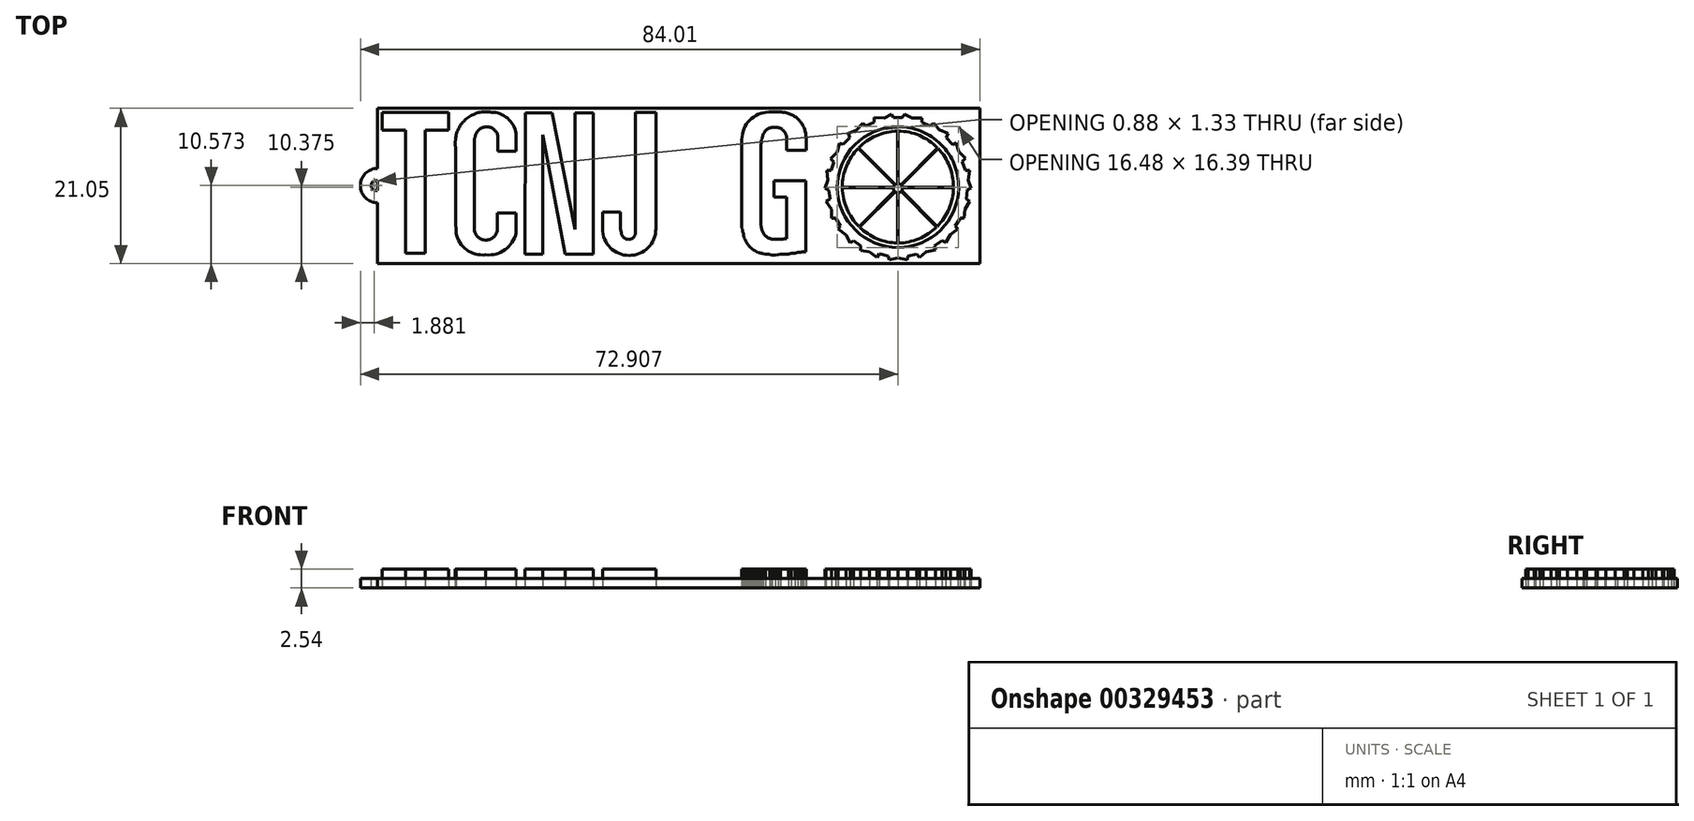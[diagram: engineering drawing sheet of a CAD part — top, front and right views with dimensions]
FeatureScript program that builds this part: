
annotation { "Feature Type Name" : "Feature", "Feature Type Description" : "" }
export const myFeature = defineFeature(function(context is Context, id is Id, definition is map)
    precondition{}
    {
        {
            var Q0;
            Q0=qCreatedBy(makeId("Top.planeOp"),FACE);
            var sketch = newSketch(context, id + "F0", { "sketchPlane" : qUnion([Q0])});
            skLineSegment(sketch, "E0", {"start": v(-44.56, 10.68) * mm, "end": v(-35.54, 10.68) * mm});
            skLineSegment(sketch, "E1", {"start": v(-35.54, 8.27) * mm, "end": v(-38.72, 8.27) * mm});
            skLineSegment(sketch, "E2", {"start": v(-38.72, 8.27) * mm, "end": v(-38.72, -8.39) * mm});
            skLineSegment(sketch, "E3", {"start": v(-38.72, -8.39) * mm, "end": v(-41.34, -8.39) * mm});
            skLineSegment(sketch, "E4", {"start": v(-41.34, -8.39) * mm, "end": v(-41.34, 8.27) * mm});
            skLineSegment(sketch, "E5", {"start": v(-44.56, 10.68) * mm, "end": v(-44.56, 8.3) * mm});
            skLineSegment(sketch, "E6", {"start": v(-44.56, 8.3) * mm, "end": v(-41.34, 8.27) * mm});
            skLineSegment(sketch, "E7", {"start": v(-35.54, 10.68) * mm, "end": v(-35.54, 8.27) * mm});
            skLineSegment(sketch, "E8", {"start": v(-28.83, 5.45) * mm, "end": v(-26.4, 5.45) * mm});
            skLineSegment(sketch, "E9", {"start": v(-26.4, 5.45) * mm, "end": v(-26.4, 7.84) * mm});
            skArc(sketch, "E10", {"start": v(-26.4, 7.84) * mm, "mid": v(-27.53, 9.9) * mm, "end": v(-29.75, 10.73) * mm});
            skArc(sketch, "E11", {"start": v(-29.75, 10.73) * mm, "mid": v(-32.98, 9.95) * mm, "end": v(-34.6, 7.04) * mm});
            skArc(sketch, "E12", {"start": v(-34.6, 7.04) * mm, "mid": v(-34.62, 6.47) * mm, "end": v(-34.6, 5.9) * mm});
            skLineSegment(sketch, "E13", {"start": v(-34.6, 5.9) * mm, "end": v(-34.6, -3.94) * mm});
            skArc(sketch, "E14", {"start": v(-28.83, 7.44) * mm, "mid": v(-30.37, 8.75) * mm, "end": v(-31.9, 7.43) * mm});
            skLineSegment(sketch, "E15", {"start": v(-28.83, 7.44) * mm, "end": v(-28.83, 5.45) * mm});
            skArc(sketch, "E16", {"start": v(-31.9, 7.43) * mm, "mid": v(-32.02, 7.1) * mm, "end": v(-32.05, 6.76) * mm});
            skLineSegment(sketch, "E17", {"start": v(-32.05, 6.76) * mm, "end": v(-32.05, -3.9) * mm});
            skLineSegment(sketch, "E18", {"start": v(-32.05, -3.9) * mm, "end": v(-32.05, -5.06) * mm});
            skArc(sketch, "E19", {"start": v(-32.05, -5.06) * mm, "mid": v(-30.48, -6.63) * mm, "end": v(-28.9, -5.06) * mm});
            skLineSegment(sketch, "E20", {"start": v(-28.9, -5.06) * mm, "end": v(-28.9, -2.93) * mm});
            skLineSegment(sketch, "E21", {"start": v(-28.9, -2.93) * mm, "end": v(-26.38, -2.93) * mm});
            skLineSegment(sketch, "E22", {"start": v(-26.38, -2.93) * mm, "end": v(-26.38, -5.66) * mm});
            skArc(sketch, "E23", {"start": v(-30.48, -8.61) * mm, "mid": v(-27.86, -7.93) * mm, "end": v(-26.38, -5.66) * mm});
            skArc(sketch, "E24", {"start": v(-34.5, -5.66) * mm, "mid": v(-33.08, -7.94) * mm, "end": v(-30.48, -8.61) * mm});
            skLineSegment(sketch, "E25", {"start": v(-34.6, -3.94) * mm, "end": v(-34.5, -5.66) * mm});
            skLineSegment(sketch, "E26", {"start": v(-25.23, 10.62) * mm, "end": v(-21.47, 10.62) * mm});
            skLineSegment(sketch, "E27", {"start": v(-21.47, 10.62) * mm, "end": v(-18.35, -5.14) * mm});
            skLineSegment(sketch, "E28", {"start": v(-18.35, -5.14) * mm, "end": v(-18.35, 10.66) * mm});
            skLineSegment(sketch, "E29", {"start": v(-18.35, 10.66) * mm, "end": v(-15.87, 10.66) * mm});
            skLineSegment(sketch, "E30", {"start": v(-15.87, 10.66) * mm, "end": v(-15.87, -8.5) * mm});
            skLineSegment(sketch, "E31", {"start": v(-15.87, -8.5) * mm, "end": v(-19.7, -8.5) * mm});
            skLineSegment(sketch, "E32", {"start": v(-19.7, -8.5) * mm, "end": v(-22.75, 7.66) * mm});
            skLineSegment(sketch, "E33", {"start": v(-22.75, 7.66) * mm, "end": v(-22.75, -8.5) * mm});
            skLineSegment(sketch, "E34", {"start": v(-22.75, -8.5) * mm, "end": v(-25.19, -8.5) * mm});
            skLineSegment(sketch, "E35", {"start": v(-25.19, -8.5) * mm, "end": v(-25.11, 10.62) * mm});
            skLineSegment(sketch, "E36", {"start": v(-10.17, 10.7) * mm, "end": v(-7.42, 10.7) * mm});
            skLineSegment(sketch, "E37", {"start": v(-7.42, 10.7) * mm, "end": v(-7.42, -5.1) * mm});
            skArc(sketch, "E38", {"start": v(-14.65, -5.1) * mm, "mid": v(-11.03, -8.7) * mm, "end": v(-7.42, -5.1) * mm});
            skLineSegment(sketch, "E39", {"start": v(-14.65, -5.1) * mm, "end": v(-14.65, -2.85) * mm});
            skLineSegment(sketch, "E40", {"start": v(-14.65, -2.85) * mm, "end": v(-12.2, -2.85) * mm});
            skLineSegment(sketch, "E41", {"start": v(-12.2, -2.85) * mm, "end": v(-12.2, -5.1) * mm});
            skLineSegment(sketch, "E42", {"start": v(-10.17, 10.7) * mm, "end": v(-10.17, -5.1) * mm});
            skLineSegment(sketch, "E43", {"start": v(-12.2, -5.1) * mm, "end": v(-12.11, -5.6) * mm});
            skLineSegment(sketch, "E44", {"start": v(-10.17, -5.1) * mm, "end": v(-10.17, -5.57) * mm});
            skArc(sketch, "E45", {"start": v(-12.11, -5.6) * mm, "mid": v(-11.12, -6.54) * mm, "end": v(-10.17, -5.57) * mm});
            skLineSegment(sketch, "E46", {"start": v(10.32, 5.53) * mm, "end": v(12.96, 5.53) * mm});
            skLineSegment(sketch, "E47", {"start": v(12.96, 5.53) * mm, "end": v(12.96, 7.18) * mm});
            skLineSegment(sketch, "E48", {"start": v(10.32, 5.53) * mm, "end": v(10.32, 7.18) * mm});
            skLineSegment(sketch, "E49", {"start": v(7.88, 10.74) * mm, "end": v(9.46, 10.74) * mm});
            skArc(sketch, "E50", {"start": v(12.96, 7.18) * mm, "mid": v(11.96, 9.7) * mm, "end": v(9.46, 10.74) * mm});
            skLineSegment(sketch, "E51", {"start": v(6.83, 6.3) * mm, "end": v(6.83, -4.43) * mm});
            skLineSegment(sketch, "E52", {"start": v(4.25, 7.04) * mm, "end": v(4.25, -4.85) * mm});
            skLineSegment(sketch, "E53", {"start": v(9.86, -6.5) * mm, "end": v(8.28, -6.5) * mm});
            skLineSegment(sketch, "E54", {"start": v(9.86, -6.5) * mm, "end": v(9.96, -6.44) * mm});
            skLineSegment(sketch, "E55", {"start": v(9.96, -6.44) * mm, "end": v(10.32, -6.44) * mm});
            skLineSegment(sketch, "E56", {"start": v(10.32, -6.44) * mm, "end": v(10.32, -0.84) * mm});
            skLineSegment(sketch, "E57", {"start": v(10.32, -0.84) * mm, "end": v(10.32, -0.8) * mm});
            skLineSegment(sketch, "E58", {"start": v(10.32, -0.8) * mm, "end": v(8.58, -0.8) * mm});
            skLineSegment(sketch, "E59", {"start": v(8.58, -0.8) * mm, "end": v(8.58, 1.43) * mm});
            skLineSegment(sketch, "E60", {"start": v(8.58, 1.43) * mm, "end": v(12.92, 1.43) * mm});
            skLineSegment(sketch, "E61", {"start": v(12.92, 1.43) * mm, "end": v(12.92, -8.2) * mm});
            skLineSegment(sketch, "E62", {"start": v(12.92, -8.2) * mm, "end": v(12.6, -8.2) * mm});
            skLineSegment(sketch, "E63", {"start": v(12.6, -8.2) * mm, "end": v(12.44, -8.25) * mm});
            skLineSegment(sketch, "E64", {"start": v(12.44, -8.25) * mm, "end": v(12.24, -8.3) * mm});
            skLineSegment(sketch, "E65", {"start": v(12.24, -8.3) * mm, "end": v(11.83, -8.3) * mm});
            skLineSegment(sketch, "E66", {"start": v(11.83, -8.3) * mm, "end": v(11.61, -8.38) * mm});
            skLineSegment(sketch, "E67", {"start": v(11.61, -8.38) * mm, "end": v(11.48, -8.42) * mm});
            skLineSegment(sketch, "E68", {"start": v(11.48, -8.42) * mm, "end": v(11.08, -8.42) * mm});
            skLineSegment(sketch, "E69", {"start": v(11.08, -8.42) * mm, "end": v(10.99, -8.42) * mm});
            skLineSegment(sketch, "E70", {"start": v(10.99, -8.42) * mm, "end": v(10.95, -8.42) * mm});
            skLineSegment(sketch, "E71", {"start": v(10.95, -8.42) * mm, "end": v(10.6, -8.54) * mm});
            skLineSegment(sketch, "E72", {"start": v(10.6, -8.54) * mm, "end": v(9.46, -8.54) * mm});
            skLineSegment(sketch, "E73", {"start": v(9.46, -8.54) * mm, "end": v(9.16, -8.58) * mm});
            skLineSegment(sketch, "E74", {"start": v(9.16, -8.58) * mm, "end": v(8.82, -8.65) * mm});
            skLineSegment(sketch, "E75", {"start": v(8.82, -8.65) * mm, "end": v(8.36, -8.65) * mm});
            skLineSegment(sketch, "E76", {"start": v(8.36, -8.65) * mm, "end": v(8.12, -8.58) * mm});
            skLineSegment(sketch, "E77", {"start": v(8.12, -8.58) * mm, "end": v(8.04, -8.55) * mm});
            skLineSegment(sketch, "E78", {"start": v(8.04, -8.55) * mm, "end": v(7.44, -8.55) * mm});
            skLineSegment(sketch, "E79", {"start": v(7.44, -8.55) * mm, "end": v(7.13, -8.45) * mm});
            skLineSegment(sketch, "E80", {"start": v(7.13, -8.45) * mm, "end": v(7.09, -8.43) * mm});
            skLineSegment(sketch, "E81", {"start": v(7.09, -8.43) * mm, "end": v(6.83, -8.43) * mm});
            skLineSegment(sketch, "E82", {"start": v(6.83, -8.43) * mm, "end": v(6.67, -8.32) * mm});
            skLineSegment(sketch, "E83", {"start": v(6.67, -8.32) * mm, "end": v(6.52, -8.32) * mm});
            skLineSegment(sketch, "E84", {"start": v(6.52, -8.32) * mm, "end": v(6.34, -8.21) * mm});
            skLineSegment(sketch, "E85", {"start": v(6.34, -8.21) * mm, "end": v(6.22, -8.21) * mm});
            skLineSegment(sketch, "E86", {"start": v(6.22, -8.21) * mm, "end": v(6.19, -8.16) * mm});
            skLineSegment(sketch, "E87", {"start": v(6.19, -8.16) * mm, "end": v(6.1, -8.09) * mm});
            skLineSegment(sketch, "E88", {"start": v(6.1, -8.09) * mm, "end": v(6, -8.09) * mm});
            skLineSegment(sketch, "E89", {"start": v(6, -8.09) * mm, "end": v(5.87, -7.97) * mm});
            skLineSegment(sketch, "E90", {"start": v(5.87, -7.97) * mm, "end": v(5.77, -7.94) * mm});
            skLineSegment(sketch, "E91", {"start": v(5.77, -7.94) * mm, "end": v(5.74, -7.85) * mm});
            skLineSegment(sketch, "E92", {"start": v(5.74, -7.85) * mm, "end": v(5.63, -7.85) * mm});
            skLineSegment(sketch, "E93", {"start": v(5.63, -7.85) * mm, "end": v(5.6, -7.74) * mm});
            skLineSegment(sketch, "E94", {"start": v(5.6, -7.74) * mm, "end": v(5.5, -7.74) * mm});
            skLineSegment(sketch, "E95", {"start": v(5.5, -7.74) * mm, "end": v(5.47, -7.64) * mm});
            skLineSegment(sketch, "E96", {"start": v(5.47, -7.64) * mm, "end": v(5.4, -7.64) * mm});
            skLineSegment(sketch, "E97", {"start": v(5.4, -7.64) * mm, "end": v(5.29, -7.53) * mm});
            skLineSegment(sketch, "E98", {"start": v(5.29, -7.53) * mm, "end": v(5.29, -7.48) * mm});
            skLineSegment(sketch, "E99", {"start": v(5.29, -7.48) * mm, "end": v(5.18, -7.38) * mm});
            skLineSegment(sketch, "E100", {"start": v(5.18, -7.38) * mm, "end": v(5.15, -7.38) * mm});
            skLineSegment(sketch, "E101", {"start": v(5.15, -7.38) * mm, "end": v(5.15, -7.33) * mm});
            skLineSegment(sketch, "E102", {"start": v(5.15, -7.33) * mm, "end": v(5.05, -7.26) * mm});
            skLineSegment(sketch, "E103", {"start": v(5.05, -7.26) * mm, "end": v(5.05, -7.14) * mm});
            skLineSegment(sketch, "E104", {"start": v(5.05, -7.14) * mm, "end": v(4.93, -7.03) * mm});
            skLineSegment(sketch, "E105", {"start": v(4.93, -7.03) * mm, "end": v(4.93, -6.95) * mm});
            skLineSegment(sketch, "E106", {"start": v(4.93, -6.95) * mm, "end": v(4.8, -6.87) * mm});
            skLineSegment(sketch, "E107", {"start": v(4.8, -6.87) * mm, "end": v(4.8, -6.75) * mm});
            skLineSegment(sketch, "E108", {"start": v(4.8, -6.75) * mm, "end": v(4.7, -6.65) * mm});
            skLineSegment(sketch, "E109", {"start": v(4.7, -6.65) * mm, "end": v(4.7, -6.51) * mm});
            skLineSegment(sketch, "E110", {"start": v(4.7, -6.51) * mm, "end": v(4.56, -6.34) * mm});
            skLineSegment(sketch, "E111", {"start": v(4.56, -6.34) * mm, "end": v(4.56, -6.19) * mm});
            skLineSegment(sketch, "E112", {"start": v(4.56, -6.19) * mm, "end": v(4.45, -6.1) * mm});
            skLineSegment(sketch, "E113", {"start": v(4.45, -6.1) * mm, "end": v(4.45, -5.75) * mm});
            skLineSegment(sketch, "E114", {"start": v(4.45, -5.75) * mm, "end": v(4.33, -5.48) * mm});
            skLineSegment(sketch, "E115", {"start": v(4.33, -5.48) * mm, "end": v(4.33, -5.18) * mm});
            skLineSegment(sketch, "E116", {"start": v(4.33, -5.18) * mm, "end": v(4.25, -4.97) * mm});
            skLineSegment(sketch, "E117", {"start": v(4.25, -4.97) * mm, "end": v(4.25, -4.85) * mm});
            skLineSegment(sketch, "E118", {"start": v(6.83, -4.43) * mm, "end": v(6.9, -5) * mm});
            skArc(sketch, "E119", {"start": v(6.9, -5) * mm, "mid": v(7.36, -5.96) * mm, "end": v(8.28, -6.5) * mm});
            skArc(sketch, "E120", {"start": v(7.88, 10.74) * mm, "mid": v(5.3, 9.63) * mm, "end": v(4.25, 7.04) * mm});
            skLineSegment(sketch, "E121", {"start": v(8.3, 8.66) * mm, "end": v(9.14, 8.66) * mm});
            skArc(sketch, "E122", {"start": v(10.32, 7.18) * mm, "mid": v(9.99, 8.13) * mm, "end": v(9.14, 8.66) * mm});
            skLineSegment(sketch, "E123", {"start": v(6.83, 6.3) * mm, "end": v(6.9, 6.58) * mm});
            skLineSegment(sketch, "E124", {"start": v(6.9, 6.58) * mm, "end": v(6.9, 6.96) * mm});
            skLineSegment(sketch, "E125", {"start": v(6.9, 6.96) * mm, "end": v(7.02, 7.18) * mm});
            skArc(sketch, "E126", {"start": v(8.3, 8.66) * mm, "mid": v(7.4, 8.15) * mm, "end": v(7.02, 7.18) * mm});
            skLineSegment(sketch, "E127", {"start": v(25.99, 9.98) * mm, "end": v(26.33, 10.46) * mm});
            skLineSegment(sketch, "E128", {"start": v(26.33, 10.46) * mm, "end": v(27.34, 9.96) * mm});
            skLineSegment(sketch, "E129", {"start": v(27.34, 9.96) * mm, "end": v(28.66, 9.96) * mm});
            skLineSegment(sketch, "E130", {"start": v(28.66, 9.96) * mm, "end": v(28.66, 9.39) * mm});
            skLineSegment(sketch, "E131", {"start": v(28.66, 9.39) * mm, "end": v(29.76, 8.84) * mm});
            skLineSegment(sketch, "E132", {"start": v(29.76, 8.84) * mm, "end": v(30.25, 9.25) * mm});
            skLineSegment(sketch, "E133", {"start": v(31, 8.32) * mm, "end": v(30.25, 9.25) * mm});
            skLineSegment(sketch, "E134", {"start": v(31, 8.32) * mm, "end": v(32.22, 7.85) * mm});
            skLineSegment(sketch, "E135", {"start": v(32.22, 7.85) * mm, "end": v(32, 7.3) * mm});
            skLineSegment(sketch, "E136", {"start": v(32, 7.3) * mm, "end": v(32.78, 6.39) * mm});
            skLineSegment(sketch, "E137", {"start": v(33.3, 6.59) * mm, "end": v(32.85, 6.31) * mm});
            skLineSegment(sketch, "E138", {"start": v(32.85, 6.31) * mm, "end": v(32.78, 6.39) * mm});
            skLineSegment(sketch, "E139", {"start": v(25.99, 9.98) * mm, "end": v(24.82, 9.98) * mm});
            skLineSegment(sketch, "E140", {"start": v(24.82, 9.98) * mm, "end": v(24.57, 10.46) * mm});
            skLineSegment(sketch, "E141", {"start": v(24.57, 10.46) * mm, "end": v(23.6, 9.95) * mm});
            skLineSegment(sketch, "E142", {"start": v(23.6, 9.95) * mm, "end": v(22.2, 9.98) * mm});
            skLineSegment(sketch, "E143", {"start": v(22.2, 9.98) * mm, "end": v(22.2, 9.39) * mm});
            skLineSegment(sketch, "E144", {"start": v(22.2, 9.39) * mm, "end": v(21.05, 8.85) * mm});
            skLineSegment(sketch, "E145", {"start": v(21.05, 8.85) * mm, "end": v(20.66, 9.22) * mm});
            skLineSegment(sketch, "E146", {"start": v(20.66, 9.22) * mm, "end": v(19.8, 8.31) * mm});
            skLineSegment(sketch, "E147", {"start": v(19.8, 8.31) * mm, "end": v(18.68, 7.83) * mm});
            skLineSegment(sketch, "E148", {"start": v(18.68, 7.83) * mm, "end": v(18.9, 7.3) * mm});
            skLineSegment(sketch, "E149", {"start": v(18.9, 7.3) * mm, "end": v(18.02, 6.36) * mm});
            skLineSegment(sketch, "E150", {"start": v(18.02, 6.36) * mm, "end": v(17.47, 6.5) * mm});
            skLineSegment(sketch, "E151", {"start": v(17.47, 6.5) * mm, "end": v(17.15, 5.3) * mm});
            skLineSegment(sketch, "E152", {"start": v(17.15, 5.3) * mm, "end": v(16.29, 4.39) * mm});
            skLineSegment(sketch, "E153", {"start": v(16.29, 4.39) * mm, "end": v(16.72, 3.98) * mm});
            skLineSegment(sketch, "E154", {"start": v(16.72, 3.98) * mm, "end": v(16.37, 2.85) * mm});
            skLineSegment(sketch, "E155", {"start": v(16.37, 2.85) * mm, "end": v(15.76, 2.8) * mm});
            skLineSegment(sketch, "E156", {"start": v(15.76, 2.8) * mm, "end": v(15.92, 1.52) * mm});
            skLineSegment(sketch, "E157", {"start": v(15.92, 1.52) * mm, "end": v(15.5, 0.39) * mm});
            skLineSegment(sketch, "E158", {"start": v(15.5, 0.39) * mm, "end": v(16.03, 0.19) * mm});
            skLineSegment(sketch, "E159", {"start": v(16.03, 0.19) * mm, "end": v(16.2, -1.04) * mm});
            skLineSegment(sketch, "E160", {"start": v(16.2, -1.04) * mm, "end": v(15.65, -1.34) * mm});
            skLineSegment(sketch, "E161", {"start": v(15.65, -1.34) * mm, "end": v(16.42, -2.43) * mm});
            skLineSegment(sketch, "E162", {"start": v(16.42, -2.43) * mm, "end": v(16.42, -3.68) * mm});
            skLineSegment(sketch, "E163", {"start": v(16.42, -3.68) * mm, "end": v(16.99, -3.68) * mm});
            skLineSegment(sketch, "E164", {"start": v(16.99, -3.68) * mm, "end": v(17.6, -4.71) * mm});
            skLineSegment(sketch, "E165", {"start": v(17.6, -4.71) * mm, "end": v(17.31, -5.13) * mm});
            skLineSegment(sketch, "E166", {"start": v(17.31, -5.13) * mm, "end": v(18.38, -5.94) * mm});
            skLineSegment(sketch, "E167", {"start": v(18.38, -5.94) * mm, "end": v(18.94, -6.99) * mm});
            skLineSegment(sketch, "E168", {"start": v(18.94, -6.99) * mm, "end": v(19.42, -6.7) * mm});
            skLineSegment(sketch, "E169", {"start": v(19.42, -6.7) * mm, "end": v(20.35, -7.4) * mm});
            skLineSegment(sketch, "E170", {"start": v(20.35, -7.4) * mm, "end": v(20.35, -8.03) * mm});
            skLineSegment(sketch, "E171", {"start": v(20.35, -8.03) * mm, "end": v(21.56, -8.22) * mm});
            skLineSegment(sketch, "E172", {"start": v(21.56, -8.22) * mm, "end": v(22.54, -8.97) * mm});
            skLineSegment(sketch, "E173", {"start": v(22.54, -8.97) * mm, "end": v(22.9, -8.49) * mm});
            skLineSegment(sketch, "E174", {"start": v(22.9, -8.49) * mm, "end": v(24.13, -8.78) * mm});
            skLineSegment(sketch, "E175", {"start": v(24.13, -8.78) * mm, "end": v(24.21, -9.32) * mm});
            skLineSegment(sketch, "E176", {"start": v(24.21, -9.32) * mm, "end": v(25.45, -9.08) * mm});
            skLineSegment(sketch, "E177", {"start": v(25.45, -9.08) * mm, "end": v(26.68, -9.33) * mm});
            skLineSegment(sketch, "E178", {"start": v(26.68, -9.33) * mm, "end": v(26.8, -8.76) * mm});
            skLineSegment(sketch, "E179", {"start": v(26.8, -8.76) * mm, "end": v(27.97, -8.54) * mm});
            skLineSegment(sketch, "E180", {"start": v(27.97, -8.54) * mm, "end": v(28.38, -8.97) * mm});
            skLineSegment(sketch, "E181", {"start": v(28.38, -8.97) * mm, "end": v(29.26, -8.2) * mm});
            skLineSegment(sketch, "E182", {"start": v(29.26, -8.2) * mm, "end": v(30.49, -7.98) * mm});
            skLineSegment(sketch, "E183", {"start": v(30.49, -7.98) * mm, "end": v(30.4, -7.43) * mm});
            skLineSegment(sketch, "E184", {"start": v(30.4, -7.43) * mm, "end": v(31.39, -6.68) * mm});
            skLineSegment(sketch, "E185", {"start": v(31.39, -6.68) * mm, "end": v(31.9, -6.96) * mm});
            skLineSegment(sketch, "E186", {"start": v(31.9, -6.96) * mm, "end": v(32.54, -5.9) * mm});
            skLineSegment(sketch, "E187", {"start": v(32.54, -5.9) * mm, "end": v(33.56, -5.13) * mm});
            skLineSegment(sketch, "E188", {"start": v(33.56, -5.13) * mm, "end": v(33.21, -4.73) * mm});
            skLineSegment(sketch, "E189", {"start": v(33.21, -4.73) * mm, "end": v(33.86, -3.64) * mm});
            skLineSegment(sketch, "E190", {"start": v(33.86, -3.64) * mm, "end": v(34.4, -3.64) * mm});
            skLineSegment(sketch, "E191", {"start": v(34.4, -3.64) * mm, "end": v(34.52, -2.41) * mm});
            skLineSegment(sketch, "E192", {"start": v(34.52, -2.41) * mm, "end": v(35.14, -1.38) * mm});
            skLineSegment(sketch, "E193", {"start": v(35.14, -1.38) * mm, "end": v(34.69, -1.05) * mm});
            skLineSegment(sketch, "E194", {"start": v(34.69, -1.05) * mm, "end": v(34.8, 0.2) * mm});
            skLineSegment(sketch, "E195", {"start": v(34.8, 0.2) * mm, "end": v(35.34, 0.39) * mm});
            skLineSegment(sketch, "E196", {"start": v(35.34, 0.39) * mm, "end": v(34.94, 1.53) * mm});
            skLineSegment(sketch, "E197", {"start": v(34.94, 1.53) * mm, "end": v(35.13, 2.8) * mm});
            skLineSegment(sketch, "E198", {"start": v(35.13, 2.8) * mm, "end": v(34.57, 2.8) * mm});
            skLineSegment(sketch, "E199", {"start": v(34.57, 2.8) * mm, "end": v(34.13, 4.04) * mm});
            skLineSegment(sketch, "E200", {"start": v(34.13, 4.04) * mm, "end": v(34.57, 4.48) * mm});
            skLineSegment(sketch, "E201", {"start": v(34.57, 4.48) * mm, "end": v(33.72, 5.35) * mm});
            skLineSegment(sketch, "E202", {"start": v(33.72, 5.35) * mm, "end": v(33.3, 6.59) * mm});
            skArc(sketch, "E203", {"start": v(33.66, 0.47) * mm, "mid": v(31.27, 6.35) * mm, "end": v(25.4, 8.77) * mm});
            skArc(sketch, "E204", {"start": v(25.43, -7.62) * mm, "mid": v(31.2, -5.27) * mm, "end": v(33.66, 0.47) * mm});
            skArc(sketch, "E205", {"start": v(17.18, 0.47) * mm, "mid": v(19.65, -5.26) * mm, "end": v(25.43, -7.62) * mm});
            skArc(sketch, "E206", {"start": v(25.4, 8.77) * mm, "mid": v(19.58, 6.3) * mm, "end": v(17.18, 0.47) * mm});
            skArc(sketch, "E207", {"start": v(25.4, 8.17) * mm, "mid": v(20.05, 5.86) * mm, "end": v(17.87, 0.46) * mm});
            skArc(sketch, "E208", {"start": v(32.94, 0.5) * mm, "mid": v(30.77, 5.92) * mm, "end": v(25.4, 8.17) * mm});
            skArc(sketch, "E209", {"start": v(25.41, -7.04) * mm, "mid": v(30.71, -4.8) * mm, "end": v(32.94, 0.5) * mm});
            skArc(sketch, "E210", {"start": v(17.87, 0.46) * mm, "mid": v(20.14, -4.8) * mm, "end": v(25.41, -7.04) * mm});
            skArc(sketch, "E211", {"start": v(25.41, -0.2) * mm, "mid": v(25.87, 0.01) * mm, "end": v(26, 0.5) * mm});
            skArc(sketch, "E212", {"start": v(26, 0.5) * mm, "mid": v(25.81, 0.9) * mm, "end": v(25.41, 1.04) * mm});
            skArc(sketch, "E213", {"start": v(25.41, 1.04) * mm, "mid": v(25.03, 0.87) * mm, "end": v(24.82, 0.5) * mm});
            skArc(sketch, "E214", {"start": v(24.82, 0.5) * mm, "mid": v(24.95, 0.01) * mm, "end": v(25.41, -0.2) * mm});
            skLineSegment(sketch, "E215", {"start": v(17.87, 0.44) * mm, "end": v(24.81, 0.47) * mm});
            skLineSegment(sketch, "E216", {"start": v(17.87, 0.53) * mm, "end": v(24.82, 0.57) * mm});
            skLineSegment(sketch, "E217", {"start": v(24.82, 0.57) * mm, "end": v(24.84, 0.57) * mm});
            skLineSegment(sketch, "E218", {"start": v(26, 0.47) * mm, "end": v(32.94, 0.47) * mm});
            skLineSegment(sketch, "E219", {"start": v(26, 0.57) * mm, "end": v(32.94, 0.57) * mm});
            skLineSegment(sketch, "E220", {"start": v(25.81, 0.9) * mm, "end": v(30.8, 5.9) * mm});
            skLineSegment(sketch, "E221", {"start": v(25.89, 0.81) * mm, "end": v(30.87, 5.81) * mm});
            skLineSegment(sketch, "E222", {"start": v(25.37, 1.03) * mm, "end": v(25.34, 8.16) * mm});
            skLineSegment(sketch, "E223", {"start": v(25.46, 8.17) * mm, "end": v(25.46, 1.04) * mm});
            skLineSegment(sketch, "E224", {"start": v(25.08, 0.9) * mm, "end": v(20.08, 5.89) * mm});
            skLineSegment(sketch, "E225", {"start": v(20.02, 5.84) * mm, "end": v(25.02, 0.86) * mm});
            skLineSegment(sketch, "E226", {"start": v(25.37, -0.2) * mm, "end": v(25.37, -7.04) * mm});
            skLineSegment(sketch, "E227", {"start": v(25.45, -0.2) * mm, "end": v(25.45, -7.04) * mm});
            skLineSegment(sketch, "E228", {"start": v(25.03, -0.07) * mm, "end": v(20.24, -4.86) * mm});
            skLineSegment(sketch, "E229", {"start": v(20.14, -4.8) * mm, "end": v(24.95, 0.01) * mm});
            skLineSegment(sketch, "E230", {"start": v(30.67, -4.84) * mm, "end": v(25.86, 0) * mm});
            skLineSegment(sketch, "E231", {"start": v(25.92, 0.08) * mm, "end": v(30.74, -4.77) * mm});
            skLineSegment(sketch, "E232.bottom", {"start": v(-45.54, 11.75) * mm, "end": v(36.79, 11.75) * mm});
            skLineSegment(sketch, "E232.top", {"start": v(-45.54, -10.48) * mm, "end": v(36.79, -10.48) * mm});
            skLineSegment(sketch, "E232.left", {"start": v(-45.54, 11.75) * mm, "end": v(-45.54, -10.48) * mm});
            skLineSegment(sketch, "E232.right", {"start": v(36.79, 11.75) * mm, "end": v(36.79, -10.48) * mm});
            skLineSegment(sketch, "E233", {"start": v(20.24, -4.86) * mm, "end": v(20.22, -4.87) * mm});
            skSolve(sketch);
        }
        {
            var Q0;
            {var subQ0=sQuery(id+"F0.wireOp",EDGE,"E226");Q0=makeQuery(id+"F0.imprint","IMPRINT",FACE,{"disambiguationData":[TD([[makeQuery(id+"F0.imprint","IMPRINT",EDGE,{"derivedFrom":subQ0}),-1.0]])]});}
            var Q1;
            {var subQ0=sQuery(id+"F0.wireOp",EDGE,"E230");Q1=makeQuery(id+"F0.imprint","IMPRINT",FACE,{"disambiguationData":[TD([[makeQuery(id+"F0.imprint","IMPRINT",EDGE,{"derivedFrom":subQ0}),1.0]])]});}
            var Q2;
            {var subQ0=sQuery(id+"F0.wireOp",EDGE,"E231");Q2=makeQuery(id+"F0.imprint","IMPRINT",FACE,{"disambiguationData":[TD([[makeQuery(id+"F0.imprint","IMPRINT",EDGE,{"derivedFrom":subQ0}),1.0]])]});}
            var Q3;
            {var subQ0=sQuery(id+"F0.wireOp",EDGE,"E219");Q3=makeQuery(id+"F0.imprint","IMPRINT",FACE,{"disambiguationData":[TD([[makeQuery(id+"F0.imprint","IMPRINT",EDGE,{"derivedFrom":subQ0}),1.0]])]});}
            var Q4;
            {var subQ0=sQuery(id+"F0.wireOp",EDGE,"E220");Q4=makeQuery(id+"F0.imprint","IMPRINT",FACE,{"disambiguationData":[TD([[makeQuery(id+"F0.imprint","IMPRINT",EDGE,{"derivedFrom":subQ0}),1.0]])]});}
            var Q5;
            {var subQ0=sQuery(id+"F0.wireOp",EDGE,"E222");Q5=makeQuery(id+"F0.imprint","IMPRINT",FACE,{"disambiguationData":[TD([[makeQuery(id+"F0.imprint","IMPRINT",EDGE,{"derivedFrom":subQ0}),1.0]])]});}
            var Q6;
            {var subQ1=sQuery(id+"F0.wireOp",EDGE,"E216");Q6=makeQuery(id+"F0.imprint","IMPRINT",FACE,{"disambiguationData":[TD([[makeQuery(id+"F0.imprint","IMPRINT",EDGE,{"derivedFrom":subQ1}),1.0]])]});}
            var Q7;
            {var subQ0=sQuery(id+"F0.wireOp",EDGE,"E215");Q7=makeQuery(id+"F0.imprint","IMPRINT",FACE,{"disambiguationData":[TD([[makeQuery(id+"F0.imprint","IMPRINT",EDGE,{"derivedFrom":subQ0}),-1.0]])]});}
            var Q8;
            Q8=makeQuery(id+"F0.imprint","IMPRINT",FACE,{"disambiguationData":[TD([[makeQuery(id+"F0.imprint","IMPRINT",EDGE,{"derivedFrom":sQuery(id+"F0.wireOp",EDGE,"E0")}),-1.0]])]});
            var Q9;
            Q9=makeQuery(id+"F0.imprint","IMPRINT",FACE,{"disambiguationData":[TD([[makeQuery(id+"F0.imprint","IMPRINT",EDGE,{"derivedFrom":sQuery(id+"F0.wireOp",EDGE,"E8")}),1.0]])]});
            var Q10;
            {var subQ0=sQuery(id+"F0.wireOp",EDGE,"E27");Q10=makeQuery(id+"F0.imprint","IMPRINT",FACE,{"disambiguationData":[TD([[makeQuery(id+"F0.imprint","IMPRINT",EDGE,{"derivedFrom":subQ0}),-1.0]])]});}
            var Q11;
            Q11=makeQuery(id+"F0.imprint","IMPRINT",FACE,{"disambiguationData":[TD([[makeQuery(id+"F0.imprint","IMPRINT",EDGE,{"derivedFrom":sQuery(id+"F0.wireOp",EDGE,"E36")}),-1.0]])]});
            var Q12;
            Q12=makeQuery(id+"F0.imprint","IMPRINT",FACE,{"disambiguationData":[TD([[makeQuery(id+"F0.imprint","IMPRINT",EDGE,{"derivedFrom":sQuery(id+"F0.wireOp",EDGE,"E46")}),1.0]])]});
            var Q13;
            Q13=makeQuery(id+"F0.imprint","IMPRINT",FACE,{"disambiguationData":[TD([[makeQuery(id+"F0.imprint","IMPRINT",EDGE,{"derivedFrom":sQuery(id+"F0.wireOp",EDGE,"E127")}),-1.0]])]});
            extrude(context, id + "F1", {"entities" : qUnion([Q0, Q1, Q2, Q3, Q4, Q5, Q6, Q7, Q8, Q9, Q10, Q11, Q12, Q13]), "depth" : 2.54 * mm});
        }
        {
            var Q0;
            Q0=qCreatedBy(makeId("Top.planeOp"),FACE);
            var sketch = newSketch(context, id + "F2", { "sketchPlane" : qUnion([Q0])});
            skLineSegment(sketch, "E234.bottom", {"start": v(-45.17, 11.25) * mm, "end": v(36.52, 11.25) * mm});
            skLineSegment(sketch, "E234.top", {"start": v(-45.17, -9.8) * mm, "end": v(36.52, -9.8) * mm});
            skLineSegment(sketch, "E234.left", {"start": v(-45.17, 11.25) * mm, "end": v(-45.17, -9.8) * mm});
            skLineSegment(sketch, "E234.right", {"start": v(36.52, 11.25) * mm, "end": v(36.52, -9.8) * mm});
            skArc(sketch, "E235", {"start": v(-45.17, 3.11) * mm, "mid": v(-47.49, 0.77) * mm, "end": v(-45.17, -1.57) * mm});
            skArc(sketch, "E236", {"start": v(-45.17, 1.42) * mm, "mid": v(-46.05, 0.77) * mm, "end": v(-45.17, 0.13) * mm});
            skSolve(sketch);
        }
        {
            var Q0;
            Q0 = qSketchRegion(id + "F2", true);
            extrude(context, id + "F3", {"entities" : qUnion([Q0]), "depth" : 1.27 * mm});
        }
    });
